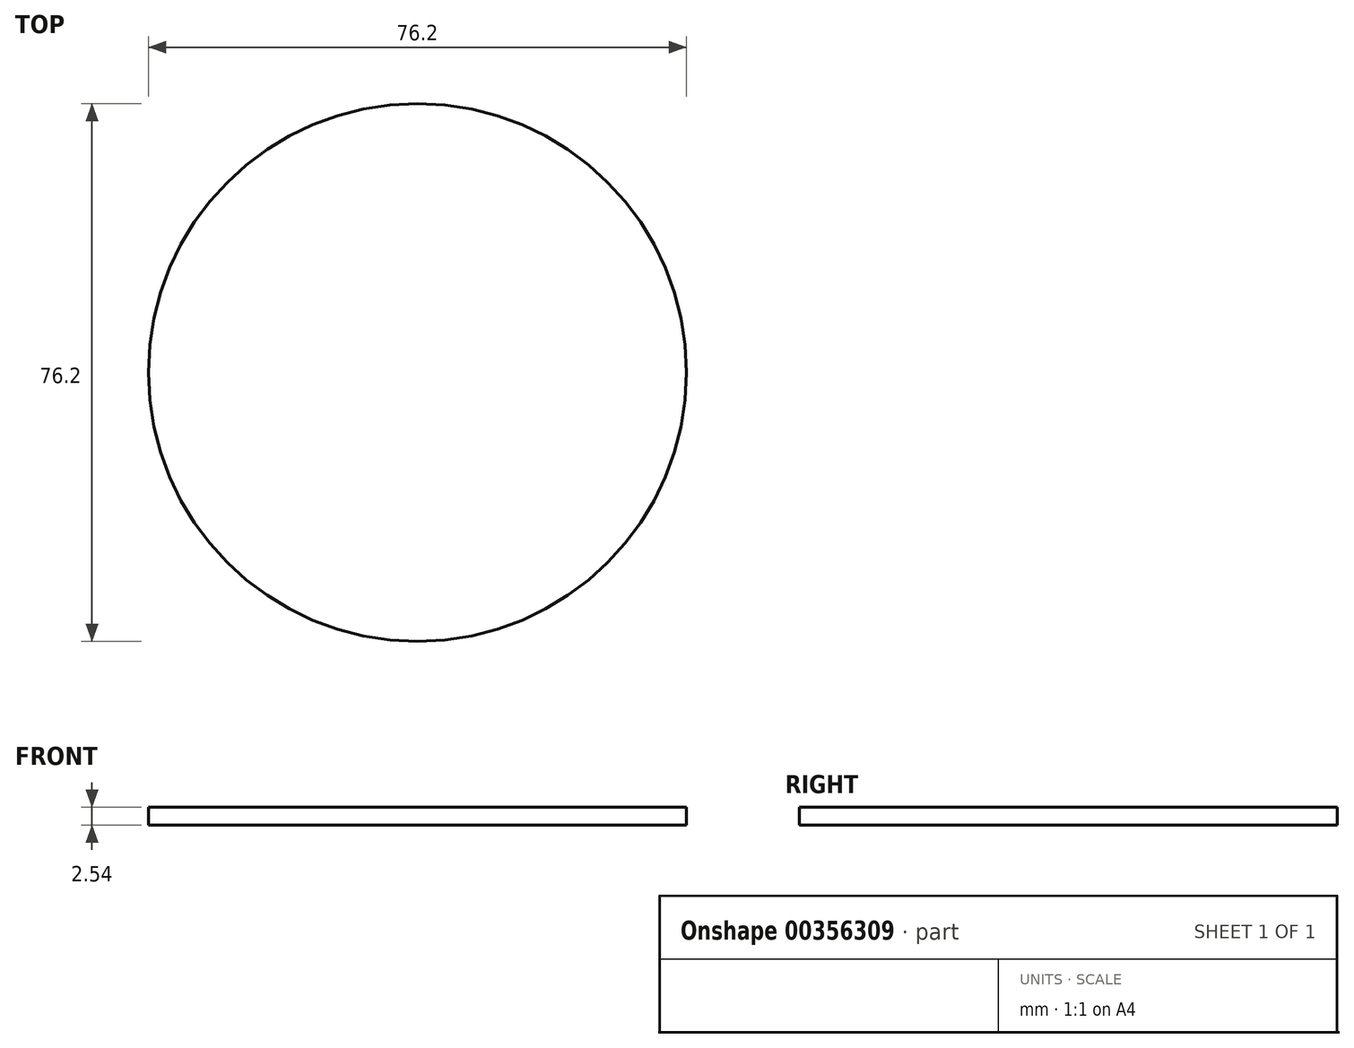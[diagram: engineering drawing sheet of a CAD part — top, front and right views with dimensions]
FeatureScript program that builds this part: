
annotation { "Feature Type Name" : "Feature", "Feature Type Description" : "" }
export const myFeature = defineFeature(function(context is Context, id is Id, definition is map)
    precondition{}
    {
        {
            var Q0;
            Q0=qCreatedBy(makeId("Top.planeOp"),FACE);
            var sketch = newSketch(context, id + "F0", { "sketchPlane" : qUnion([Q0])});
            skCircle(sketch, "E0", {"center": v(0, 0) * mm, "radius": 38.1 * mm});
            skSolve(sketch);
        }
        {
            var Q0;
            Q0=qSketchRegion(id+"F0",true);
            extrude(context, id + "F1", {"entities" : qUnion([Q0]), "endBound" : BoundingType.SYMMETRIC, "depth" : 2.54 * mm});
        }
    });
